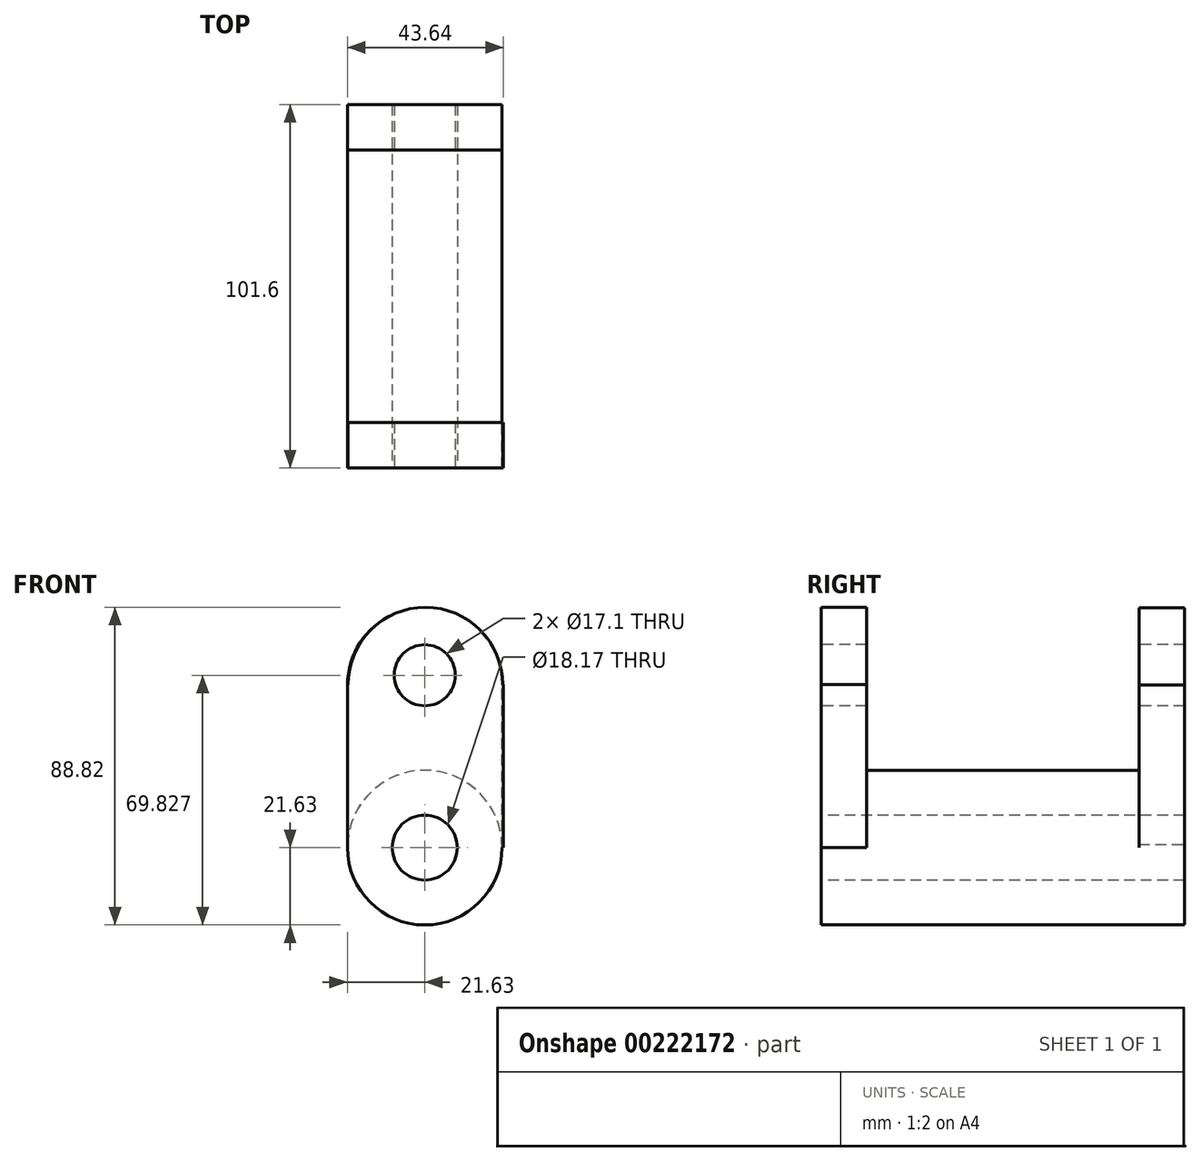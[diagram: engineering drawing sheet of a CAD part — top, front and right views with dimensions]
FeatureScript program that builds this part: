
annotation { "Feature Type Name" : "Feature", "Feature Type Description" : "" }
export const myFeature = defineFeature(function(context is Context, id is Id, definition is map)
    precondition{}
    {
        {
            var Q0;
            Q0=qCreatedBy(makeId("Front.planeOp"),FACE);
            var sketch = newSketch(context, id + "F0", { "sketchPlane" : qUnion([Q0])});
            skCircle(sketch, "E0", {"center": v(0, 0) * mm, "radius": 21.63 * mm});
            skSolve(sketch);
        }
        {
            var Q0;
            Q0 = qSketchRegion(id + "F0", true);
            extrude(context, id + "F1", {"entities" : qUnion([Q0]), "depth" : 50.8 * mm});
        }
        {
            var Q0;
            Q0=makeQuery(id+"F1.opExtrude","CAP_FACE",FACE,{"disambiguationData":[OSD([sQuery(id+"F0.wireOp",EDGE,"E0")])],"isStart":true});
            var sketch = newSketch(context, id + "F2", { "sketchPlane" : qUnion([Q0])});
            skCircle(sketch, "E1", {"center": v(0, 0) * mm, "radius": 21.64 * mm});
            skSolve(sketch);
        }
        {
            var Q0;
            Q0=makeQuery(id+"F2.imprint","IMPRINT",FACE,{"disambiguationData":[TD([[makeQuery(id+"F2.imprint","IMPRINT",EDGE,{"derivedFrom":makeQuery(id+"F1.opExtrude","CAP_EDGE",EDGE,{"disambiguationData":[OSD([sQuery(id+"F0.wireOp",EDGE,"E0")])],"isStart":true})}),-1.0]])]});
            extrude(context, id + "F3", {"entities" : qUnion([Q0]), "operationType" : NewBodyOperationType.ADD, "depth" : 50.8 * mm});
        }
        {
            var Q0;
            Q0=makeQuery(id+"F1.opExtrude","CAP_FACE",FACE,{"disambiguationData":[OSD([sQuery(id+"F0.wireOp",EDGE,"E0")])],"isStart":false});
            var sketch = newSketch(context, id + "F4", { "sketchPlane" : qUnion([Q0])});
            skLineSegment(sketch, "E2.bottom", {"start": v(-21.63, 0) * mm, "end": v(22, 0) * mm});
            skLineSegment(sketch, "E2.top", {"start": v(-21.63, 45.57) * mm, "end": v(22, 45.57) * mm});
            skLineSegment(sketch, "E2.left", {"start": v(-21.63, 0) * mm, "end": v(-21.63, 45.57) * mm});
            skLineSegment(sketch, "E2.right", {"start": v(22, 0) * mm, "end": v(22, 45.57) * mm});
            skSolve(sketch);
        }
        {
            var Q0;
            Q0 = qSketchRegion(id + "F4", true);
            extrude(context, id + "F5", {"entities" : qUnion([Q0]), "operationType" : NewBodyOperationType.ADD, "oppositeDirection" : true, "depth" : 12.7 * mm});
        }
        {
            var Q0;
            Q0=makeQuery(id+"F5.boolean.opBoolean","MERGE",FACE,{"derivedFrom":[makeQuery(id+"F1.opExtrude","CAP_FACE",FACE,{"disambiguationData":[OSD([sQuery(id+"F0.wireOp",EDGE,"E0")])],"isStart":false}),makeQuery(id+"F5.opExtrude","CAP_FACE",FACE,{"disambiguationData":[OSD([sQuery(id+"F4.wireOp",EDGE,"E2.bottom"),sQuery(id+"F4.wireOp",EDGE,"E2.top"),sQuery(id+"F4.wireOp",EDGE,"E2.left"),sQuery(id+"F4.wireOp",EDGE,"E2.right")])],"isStart":true})]});
            var sketch = newSketch(context, id + "F6", { "sketchPlane" : qUnion([Q0])});
            skCircle(sketch, "E3", {"center": v(0.19, 45.57) * mm, "radius": 21.62 * mm});
            skSolve(sketch);
        }
        {
            var Q0;
            Q0 = qSketchRegion(id + "F6", true);
            extrude(context, id + "F7", {"entities" : qUnion([Q0]), "operationType" : NewBodyOperationType.ADD, "oppositeDirection" : true, "depth" : 12.7 * mm});
        }
        {
            var Q0;
            Q0=makeQuery(id+"F3.opExtrude","CAP_FACE",FACE,{"disambiguationData":[OSD([sQuery(id+"F0.wireOp",EDGE,"E0")])],"isStart":false});
            var sketch = newSketch(context, id + "F8", { "sketchPlane" : qUnion([Q0])});
            skLineSegment(sketch, "E4.bottom", {"start": v(-21.63, 0) * mm, "end": v(21.61, 0) * mm});
            skLineSegment(sketch, "E4.top", {"start": v(-21.63, 45.5) * mm, "end": v(21.61, 45.5) * mm});
            skLineSegment(sketch, "E4.left", {"start": v(-21.63, 0) * mm, "end": v(-21.63, 45.5) * mm});
            skLineSegment(sketch, "E4.right", {"start": v(21.61, 0) * mm, "end": v(21.61, 45.5) * mm});
            skSolve(sketch);
        }
        {
            var Q0;
            Q0 = qSketchRegion(id + "F8", true);
            extrude(context, id + "F9", {"entities" : qUnion([Q0]), "operationType" : NewBodyOperationType.ADD, "oppositeDirection" : true, "depth" : 12.7 * mm});
        }
        {
            var Q0;
            Q0=makeQuery(id+"F9.boolean.opBoolean","MERGE",FACE,{"derivedFrom":[makeQuery(id+"F3.opExtrude","CAP_FACE",FACE,{"disambiguationData":[OSD([sQuery(id+"F0.wireOp",EDGE,"E0")])],"isStart":false}),makeQuery(id+"F9.opExtrude","CAP_FACE",FACE,{"disambiguationData":[OSD([sQuery(id+"F8.wireOp",EDGE,"E4.bottom"),sQuery(id+"F8.wireOp",EDGE,"E4.top"),sQuery(id+"F8.wireOp",EDGE,"E4.left"),sQuery(id+"F8.wireOp",EDGE,"E4.right")])],"isStart":true})]});
            var sketch = newSketch(context, id + "F10", { "sketchPlane" : qUnion([Q0])});
            skCircle(sketch, "E5", {"center": v(0, 45.5) * mm, "radius": 21.6 * mm});
            skSolve(sketch);
        }
        {
            var Q0;
            Q0 = qSketchRegion(id + "F10", true);
            extrude(context, id + "F11", {"entities" : qUnion([Q0]), "operationType" : NewBodyOperationType.ADD, "oppositeDirection" : true, "depth" : 12.7 * mm});
        }
        {
            var Q0;
            Q0=makeQuery(id+"F7.boolean.opBoolean","MERGE",FACE,{"derivedFrom":[makeQuery(id+"F5.boolean.opBoolean","MERGE",FACE,{"derivedFrom":[makeQuery(id+"F1.opExtrude","CAP_FACE",FACE,{"disambiguationData":[OSD([sQuery(id+"F0.wireOp",EDGE,"E0")])],"isStart":false}),makeQuery(id+"F5.opExtrude","CAP_FACE",FACE,{"disambiguationData":[OSD([sQuery(id+"F4.wireOp",EDGE,"E2.bottom"),sQuery(id+"F4.wireOp",EDGE,"E2.top"),sQuery(id+"F4.wireOp",EDGE,"E2.left"),sQuery(id+"F4.wireOp",EDGE,"E2.right")])],"isStart":true})]}),makeQuery(id+"F7.opExtrude","CAP_FACE",FACE,{"disambiguationData":[OSD([sQuery(id+"F6.wireOp",EDGE,"E3")])],"isStart":true})]});
            var sketch = newSketch(context, id + "F12", { "sketchPlane" : qUnion([Q0])});
            skCircle(sketch, "E6", {"center": v(0, 0) * mm, "radius": 9.08 * mm});
            skSolve(sketch);
        }
        {
            var Q0;
            Q0 = qSketchRegion(id + "F12", true);
            extrude(context, id + "F13", {"entities" : qUnion([Q0]), "operationType" : NewBodyOperationType.REMOVE, "endBound" : BoundingType.THROUGH_ALL, "oppositeDirection" : true, "depth" : 25.4 * mm});
        }
        {
            var Q0;
            Q0=makeQuery(id+"F7.boolean.opBoolean","MERGE",FACE,{"derivedFrom":[makeQuery(id+"F5.boolean.opBoolean","MERGE",FACE,{"derivedFrom":[makeQuery(id+"F1.opExtrude","CAP_FACE",FACE,{"disambiguationData":[OSD([sQuery(id+"F0.wireOp",EDGE,"E0")])],"isStart":false}),makeQuery(id+"F5.opExtrude","CAP_FACE",FACE,{"disambiguationData":[OSD([sQuery(id+"F4.wireOp",EDGE,"E2.bottom"),sQuery(id+"F4.wireOp",EDGE,"E2.top"),sQuery(id+"F4.wireOp",EDGE,"E2.left"),sQuery(id+"F4.wireOp",EDGE,"E2.right")])],"isStart":true})]}),makeQuery(id+"F7.opExtrude","CAP_FACE",FACE,{"disambiguationData":[OSD([sQuery(id+"F6.wireOp",EDGE,"E3")])],"isStart":true})]});
            var sketch = newSketch(context, id + "F14", { "sketchPlane" : qUnion([Q0])});
            skCircle(sketch, "E7", {"center": v(0, 48.2) * mm, "radius": 8.55 * mm});
            skSolve(sketch);
        }
        {
            var Q0;
            Q0 = qSketchRegion(id + "F14", true);
            extrude(context, id + "F15", {"entities" : qUnion([Q0]), "operationType" : NewBodyOperationType.REMOVE, "endBound" : BoundingType.THROUGH_ALL, "oppositeDirection" : true, "depth" : 25.4 * mm});
        }
    });
